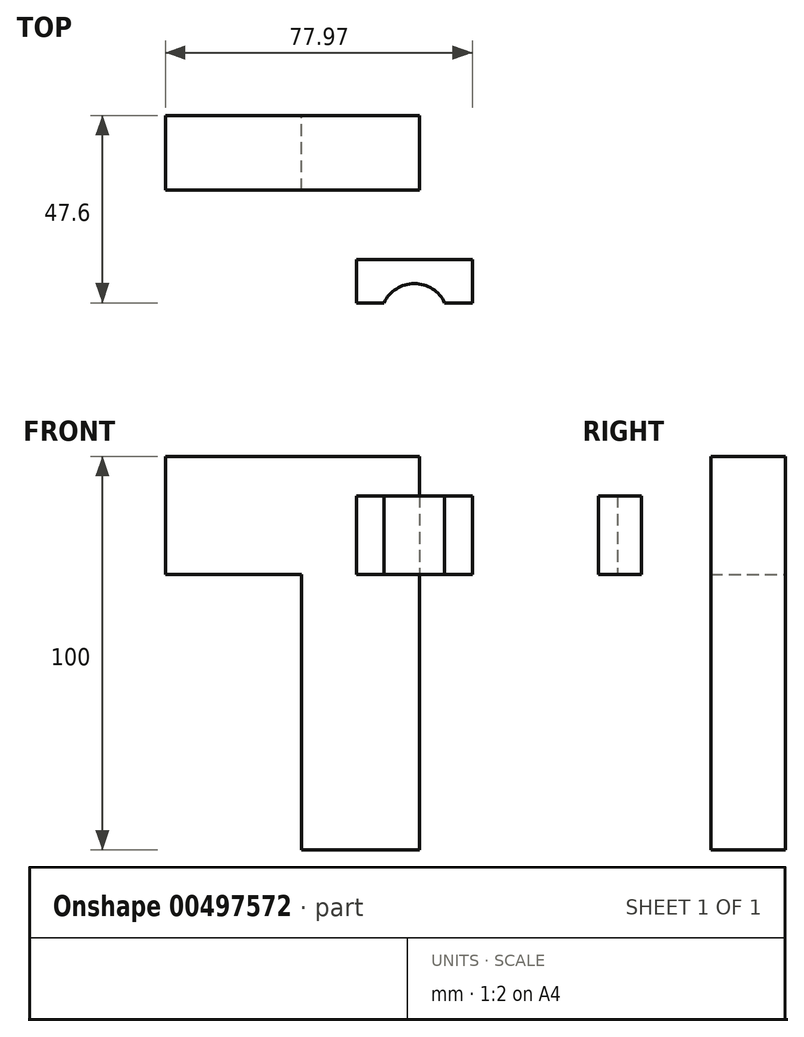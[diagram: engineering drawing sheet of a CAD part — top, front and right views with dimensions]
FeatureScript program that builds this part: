
annotation { "Feature Type Name" : "Feature", "Feature Type Description" : "" }
export const myFeature = defineFeature(function(context is Context, id is Id, definition is map)
    precondition{}
    {
        {
            var Q0;
            Q0=qCreatedBy(makeId("Front.planeOp"),FACE);
            var sketch = newSketch(context, id + "F0", { "sketchPlane" : qUnion([Q0])});
            skLineSegment(sketch, "E0.bottom", {"start": v(0, 0) * mm, "end": v(34.53, 0) * mm});
            skLineSegment(sketch, "E0.top", {"start": v(0, 30) * mm, "end": v(64.53, 30) * mm});
            skLineSegment(sketch, "E0.left", {"start": v(0, 0) * mm, "end": v(0, 30) * mm});
            skLineSegment(sketch, "E1.top", {"start": v(34.53, -70) * mm, "end": v(64.53, -70) * mm});
            skLineSegment(sketch, "E1.left", {"start": v(34.53, 0) * mm, "end": v(34.53, -70) * mm});
            skPoint(sketch, "E0.right.start.orphan", {"position": v(64.53, 0) * mm});
            skLineSegment(sketch, "E2", {"start": v(64.53, 30) * mm, "end": v(64.53, -70) * mm});
            skSolve(sketch);
        }
        {
            var Q0;
            Q0=makeQuery(id+"F0.imprint","IMPRINT",FACE,{"disambiguationData":[TD([[makeQuery(id+"F0.imprint","IMPRINT",EDGE,{"derivedFrom":sQuery(id+"F0.wireOp",EDGE,"E0.bottom")}),1.0]])]});
            extrude(context, id + "F1", {"entities" : qUnion([Q0]), "depth" : 19 * mm, "offsetDistance" : 25 * mm});
        }
        {
            var Q0;
            Q0=qCreatedBy(makeId("Top.planeOp"),FACE);
            var sketch = newSketch(context, id + "F2", { "sketchPlane" : qUnion([Q0])});
            skLineSegment(sketch, "E3", {"start": v(48.54, -36.57) * mm, "end": v(77.97, -36.57) * mm});
            skLineSegment(sketch, "E4", {"start": v(77.97, -36.57) * mm, "end": v(77.97, -47.6) * mm});
            skLineSegment(sketch, "E5", {"start": v(48.54, -36.57) * mm, "end": v(48.54, -47.6) * mm});
            skLineSegment(sketch, "E6", {"start": v(77.97, -47.6) * mm, "end": v(70.97, -47.6) * mm});
            skLineSegment(sketch, "E7", {"start": v(48.54, -47.6) * mm, "end": v(55.54, -47.6) * mm});
            skArc(sketch, "E8", {"start": v(70.97, -47.6) * mm, "mid": v(63.25, -42.7) * mm, "end": v(55.54, -47.6) * mm});
            skSolve(sketch);
        }
        {
            var Q0;
            Q0 = qSketchRegion(id + "F2", true);
            extrude(context, id + "F3", {"entities" : qUnion([Q0]), "depth" : 20 * mm, "offsetDistance" : 25 * mm});
        }
    });
